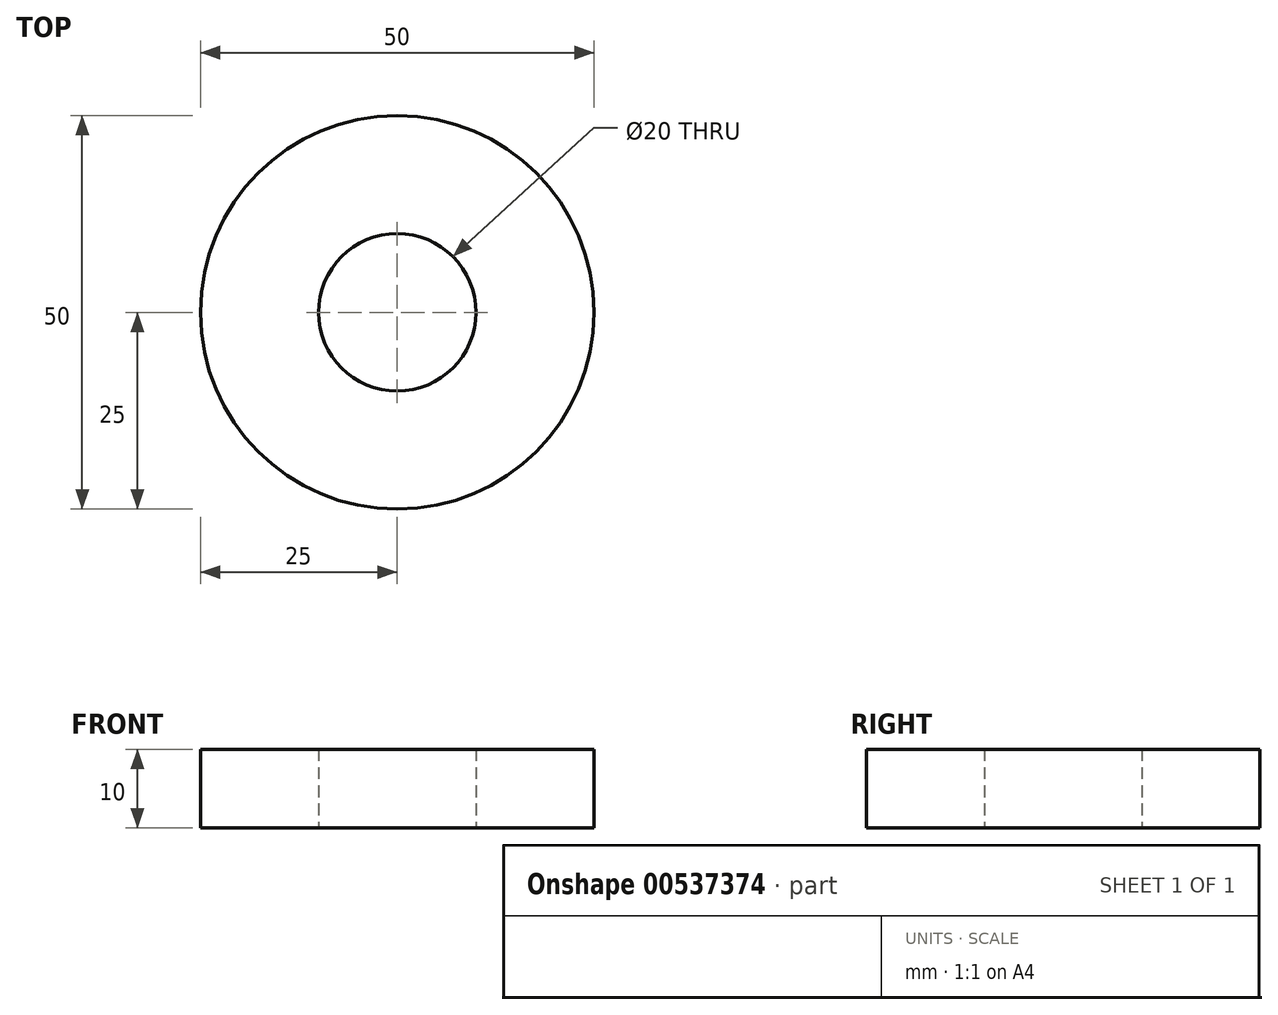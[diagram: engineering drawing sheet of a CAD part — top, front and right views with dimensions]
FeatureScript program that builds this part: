
annotation { "Feature Type Name" : "Feature", "Feature Type Description" : "" }
export const myFeature = defineFeature(function(context is Context, id is Id, definition is map)
    precondition{}
    {
        {
            var Q0;
            Q0=qCreatedBy(makeId("Top.planeOp"),FACE);
            var sketch = newSketch(context, id + "F0", { "sketchPlane" : qUnion([Q0])});
            skCircle(sketch, "E0", {"center": v(0, 0) * mm, "radius": 25 * mm});
            skCircle(sketch, "E1", {"center": v(0, 0) * mm, "radius": 10 * mm});
            skSolve(sketch);
        }
        {
            var Q0;
            Q0=qSketchRegion(id+"F0",true);
            extrude(context, id + "F1", {"entities" : qUnion([Q0]), "endBound" : BoundingType.SYMMETRIC, "depth" : 10 * mm, "offsetDistance" : 25.4 * mm});
        }
    });
